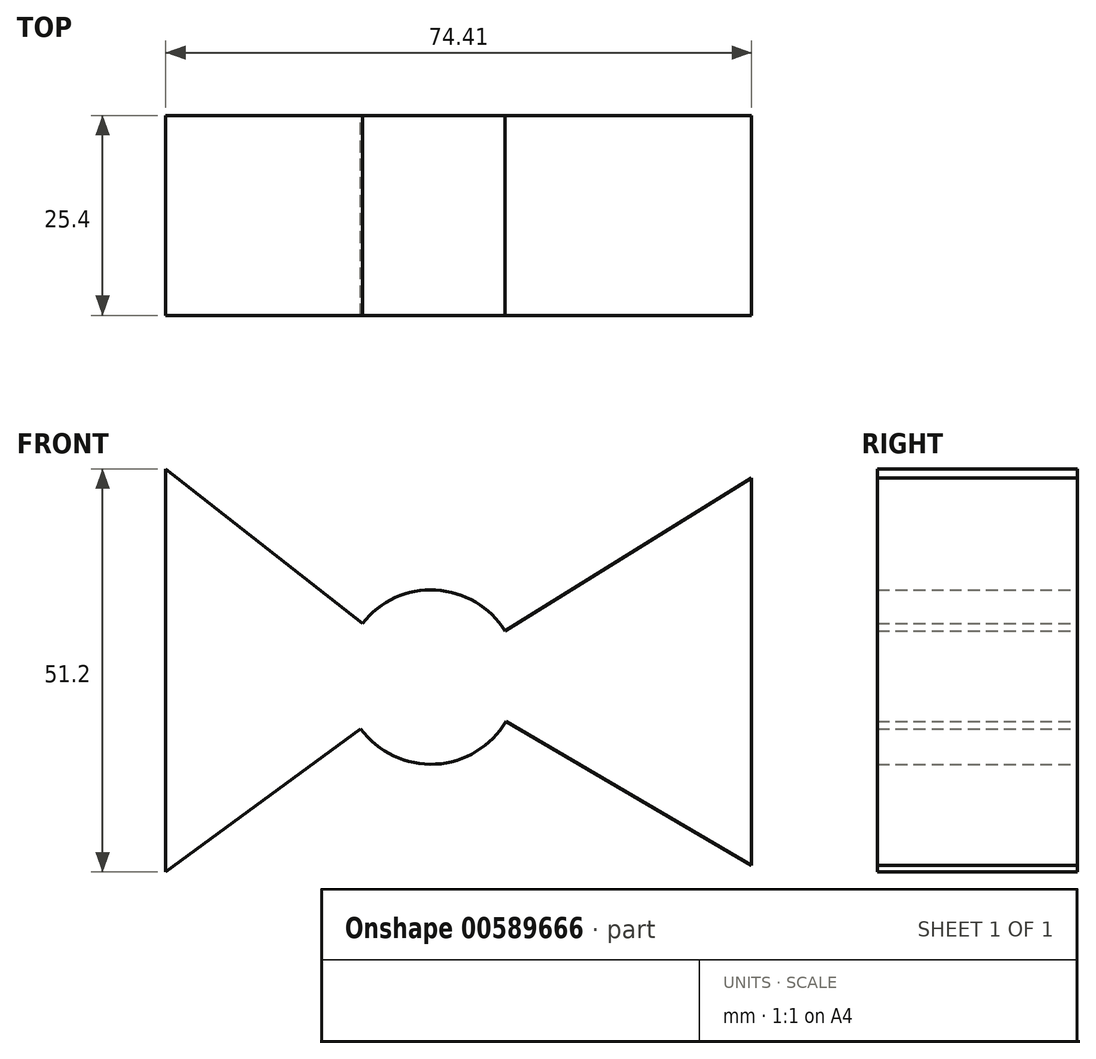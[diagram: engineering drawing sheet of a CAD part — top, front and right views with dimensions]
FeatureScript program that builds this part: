
annotation { "Feature Type Name" : "Feature", "Feature Type Description" : "" }
export const myFeature = defineFeature(function(context is Context, id is Id, definition is map)
    precondition{}
    {
        {
            var Q0;
            Q0=qCreatedBy(makeId("Front.planeOp"),FACE);
            var sketch = newSketch(context, id + "F0", { "sketchPlane" : qUnion([Q0])});
            skLineSegment(sketch, "E0", {"start": v(40.7, 25.32) * mm, "end": v(40.7, -25.04) * mm});
            skLineSegment(sketch, "E1", {"start": v(40.7, 25.32) * mm, "end": v(0, 0) * mm});
            skLineSegment(sketch, "E2", {"start": v(0, 0) * mm, "end": v(42.66, -25.04) * mm});
            skCircle(sketch, "E3", {"center": v(0, 0) * mm, "radius": 11.07 * mm});
            skLineSegment(sketch, "E4", {"start": v(0, 0) * mm, "end": v(-33.71, 26.44) * mm});
            skLineSegment(sketch, "E5", {"start": v(-33.71, 26.44) * mm, "end": v(-33.71, -24.76) * mm});
            skLineSegment(sketch, "E6", {"start": v(-33.71, -24.76) * mm, "end": v(0, 0) * mm});
            skSolve(sketch);
        }
        {
            var Q0;
            Q0 = qSketchRegion(id + "F0", true);
            extrude(context, id + "F1", {"entities" : qUnion([Q0]), "depth" : 25.4 * mm, "offsetDistance" : 25.4 * mm});
        }
    });
